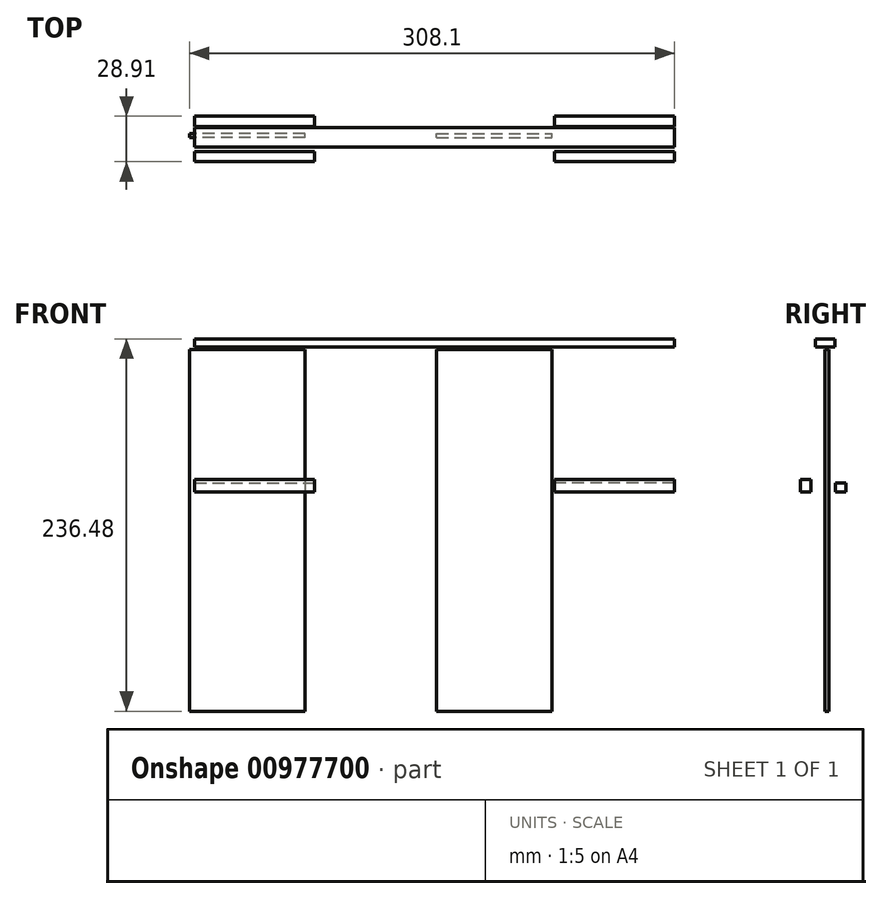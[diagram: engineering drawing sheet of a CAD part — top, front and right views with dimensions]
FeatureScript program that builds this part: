
annotation { "Feature Type Name" : "Feature", "Feature Type Description" : "" }
export const myFeature = defineFeature(function(context is Context, id is Id, definition is map)
    precondition{}
    {
        {
            var Q0;
            Q0=qCreatedBy(makeId("Front.planeOp"),FACE);
            var sketch = newSketch(context, id + "F0", { "sketchPlane" : qUnion([Q0])});
            skLineSegment(sketch, "E0.bottom", {"start": v(-73.47, 110.17) * mm, "end": v(0, 110.17) * mm});
            skLineSegment(sketch, "E0.top", {"start": v(-73.47, -119.67) * mm, "end": v(0, -119.67) * mm});
            skLineSegment(sketch, "E0.left", {"start": v(-73.47, 110.17) * mm, "end": v(-73.47, -119.67) * mm});
            skLineSegment(sketch, "E0.right", {"start": v(0, 110.17) * mm, "end": v(0, -119.67) * mm});
            skLineSegment(sketch, "E1.left", {"start": v(122.15, 40.13) * mm, "end": v(122.15, 36.44) * mm});
            skLineSegment(sketch, "E1.right", {"start": v(0, 40.13) * mm, "end": v(0, 36.44) * mm});
            skSolve(sketch);
        }
        {
            var Q0;
            {var subQ1=sQuery(id+"F0.wireOp",EDGE,"E0.bottom");Q0=makeQuery(id+"F0.imprint","IMPRINT",FACE,{"disambiguationData":[TD([[makeQuery(id+"F0.imprint","IMPRINT",EDGE,{"derivedFrom":subQ1}),-1.0]])]});}
            extrude(context, id + "F1", {"entities" : qUnion([Q0]), "depth" : 2.54 * mm, "offsetDistance" : 25.4 * mm});
        }
        {
            var Q0;
            Q0=qCreatedBy(makeId("Right.planeOp"),FACE);
            var sketch = newSketch(context, id + "F2", { "sketchPlane" : qUnion([Q0])});
            skLineSegment(sketch, "E2.bottom", {"start": v(-8.62, 111.65) * mm, "end": v(3.84, 111.65) * mm});
            skLineSegment(sketch, "E2.top", {"start": v(-8.62, 116.81) * mm, "end": v(3.84, 116.81) * mm});
            skLineSegment(sketch, "E2.left", {"start": v(-8.62, 111.65) * mm, "end": v(-8.62, 116.81) * mm});
            skLineSegment(sketch, "E2.right", {"start": v(3.84, 111.65) * mm, "end": v(3.84, 116.81) * mm});
            skSolve(sketch);
        }
        {
            var Q0;
            Q0 = qSketchRegion(id + "F2", true);
            extrude(context, id + "F3", {"entities" : qUnion([Q0]), "depth" : 152.4 * mm, "offsetDistance" : 25.4 * mm});
        }
        {
            var Q0;
            Q0=makeQuery(id+"F3.opExtrude","SWEPT_BODY",BODY,{"disambiguationData":[OSD([sQuery(id+"F2.wireOp",EDGE,"E2.bottom"),sQuery(id+"F2.wireOp",EDGE,"E2.top"),sQuery(id+"F2.wireOp",EDGE,"E2.left"),sQuery(id+"F2.wireOp",EDGE,"E2.right")])]});
            transform(context, id + "F4", {"entities" : qUnion([Q0]), "transformType" : TransformType.TRANSLATION_3D, "dx" : -76.2 * mm, "dy" : 0 * mm, "dz" : 0 * mm, "makeCopy" : false});
        }
        {
            var Q0;
            Q0=qCreatedBy(makeId("Right.planeOp"),FACE);
            var sketch = newSketch(context, id + "F5", { "sketchPlane" : qUnion([Q0])});
            skLineSegment(sketch, "E3.bottom", {"start": v(4.24, 25.3) * mm, "end": v(10.88, 25.3) * mm});
            skLineSegment(sketch, "E3.top", {"start": v(4.24, 19.45) * mm, "end": v(10.88, 19.45) * mm});
            skLineSegment(sketch, "E3.left", {"start": v(4.24, 25.3) * mm, "end": v(4.24, 19.45) * mm});
            skLineSegment(sketch, "E3.right", {"start": v(10.88, 25.3) * mm, "end": v(10.88, 19.45) * mm});
            skLineSegment(sketch, "E4.bottom", {"start": v(-18.03, 27.65) * mm, "end": v(-11.39, 27.65) * mm});
            skLineSegment(sketch, "E4.top", {"start": v(-18.03, 19.45) * mm, "end": v(-11.39, 19.45) * mm});
            skLineSegment(sketch, "E4.left", {"start": v(-18.03, 27.65) * mm, "end": v(-18.03, 19.45) * mm});
            skLineSegment(sketch, "E4.right", {"start": v(-11.39, 27.65) * mm, "end": v(-11.39, 19.45) * mm});
            skSolve(sketch);
        }
        {
            var Q0;
            Q0 = qSketchRegion(id + "F5", true);
            extrude(context, id + "F6", {"entities" : qUnion([Q0]), "depth" : 76.2 * mm, "offsetDistance" : 25.4 * mm});
        }
        {
            var Q0;
            Q0=makeQuery(id+"F1.opExtrude","SWEPT_BODY",BODY,{"disambiguationData":[OSD([sQuery(id+"F0.wireOp",EDGE,"E0.bottom"),sQuery(id+"F0.wireOp",EDGE,"E0.top"),sQuery(id+"F0.wireOp",EDGE,"E0.left"),sQuery(id+"F0.wireOp",EDGE,"E0.right"),sQuery(id+"F0.wireOp",EDGE,"E1.right")])]});
            var Q1;
            Q1=makeQuery(id+"F6.opExtrude","SWEPT_BODY",BODY,{"disambiguationData":[OSD([sQuery(id+"F5.wireOp",EDGE,"E4.bottom"),sQuery(id+"F5.wireOp",EDGE,"E4.top"),sQuery(id+"F5.wireOp",EDGE,"E4.left"),sQuery(id+"F5.wireOp",EDGE,"E4.right")])]});
            var Q2;
            Q2=makeQuery(id+"F3.opExtrude","SWEPT_BODY",BODY,{"disambiguationData":[OSD([sQuery(id+"F2.wireOp",EDGE,"E2.bottom"),sQuery(id+"F2.wireOp",EDGE,"E2.top"),sQuery(id+"F2.wireOp",EDGE,"E2.left"),sQuery(id+"F2.wireOp",EDGE,"E2.right")])]});
            var Q3;
            Q3=makeQuery(id+"F6.opExtrude","SWEPT_BODY",BODY,{"disambiguationData":[OSD([sQuery(id+"F5.wireOp",EDGE,"E3.bottom"),sQuery(id+"F5.wireOp",EDGE,"E3.top"),sQuery(id+"F5.wireOp",EDGE,"E3.left"),sQuery(id+"F5.wireOp",EDGE,"E3.right")])]});
            transform(context, id + "F7", {"entities" : qUnion([Q0, Q1, Q2, Q3]), "transformType" : TransformType.TRANSLATION_3D, "dx" : 0 * mm, "dy" : 0 * mm, "dz" : 114.3 * mm, "makeCopy" : false});
        }
        {
            var Q0;
            Q0=makeQuery(id+"F6.opExtrude","SWEPT_BODY",BODY,{"disambiguationData":[OSD([sQuery(id+"F5.wireOp",EDGE,"E4.bottom"),sQuery(id+"F5.wireOp",EDGE,"E4.top"),sQuery(id+"F5.wireOp",EDGE,"E4.left"),sQuery(id+"F5.wireOp",EDGE,"E4.right")])]});
            var Q1;
            Q1=makeQuery(id+"F1.opExtrude","SWEPT_BODY",BODY,{"disambiguationData":[OSD([sQuery(id+"F0.wireOp",EDGE,"E0.bottom"),sQuery(id+"F0.wireOp",EDGE,"E0.top"),sQuery(id+"F0.wireOp",EDGE,"E0.left"),sQuery(id+"F0.wireOp",EDGE,"E0.right"),sQuery(id+"F0.wireOp",EDGE,"E1.right")])]});
            var Q2;
            Q2=makeQuery(id+"F3.opExtrude","SWEPT_BODY",BODY,{"disambiguationData":[OSD([sQuery(id+"F2.wireOp",EDGE,"E2.bottom"),sQuery(id+"F2.wireOp",EDGE,"E2.top"),sQuery(id+"F2.wireOp",EDGE,"E2.left"),sQuery(id+"F2.wireOp",EDGE,"E2.right")])]});
            var Q3;
            Q3=makeQuery(id+"F6.opExtrude","SWEPT_BODY",BODY,{"disambiguationData":[OSD([sQuery(id+"F5.wireOp",EDGE,"E3.bottom"),sQuery(id+"F5.wireOp",EDGE,"E3.top"),sQuery(id+"F5.wireOp",EDGE,"E3.left"),sQuery(id+"F5.wireOp",EDGE,"E3.right")])]});
            var Q4;
            Q4=makeQuery(id+"F3.opExtrude","CAP_FACE",FACE,{"disambiguationData":[OSD([sQuery(id+"F2.wireOp",EDGE,"E2.bottom"),sQuery(id+"F2.wireOp",EDGE,"E2.top"),sQuery(id+"F2.wireOp",EDGE,"E2.left"),sQuery(id+"F2.wireOp",EDGE,"E2.right")])],"isStart":true});
            mirror(context, id + "F8", {"operationType" : NewBodyOperationType.ADD, "entities" : qUnion([Q0, Q1, Q2, Q3]), "mirrorPlane" : qUnion([Q4])});
        }
        {
            var Q0;
            Q0=makeQuery(id+"F1.opExtrude","SWEPT_BODY",BODY,{"disambiguationData":[OSD([sQuery(id+"F0.wireOp",EDGE,"E0.bottom"),sQuery(id+"F0.wireOp",EDGE,"E0.top"),sQuery(id+"F0.wireOp",EDGE,"E0.left"),sQuery(id+"F0.wireOp",EDGE,"E0.right"),sQuery(id+"F0.wireOp",EDGE,"E1.right")])]});
            transform(context, id + "F9", {"entities" : qUnion([Q0]), "transformType" : TransformType.TRANSLATION_3D, "dx" : 76.2 * mm, "dy" : 0 * mm, "dz" : 0 * mm, "makeCopy" : false});
        }
        {
            var Q0;
            Q0=makeQuery(id+"F1.opExtrude","SWEPT_BODY",BODY,{"disambiguationData":[OSD([sQuery(id+"F0.wireOp",EDGE,"E0.bottom"),sQuery(id+"F0.wireOp",EDGE,"E0.top"),sQuery(id+"F0.wireOp",EDGE,"E0.left"),sQuery(id+"F0.wireOp",EDGE,"E0.right"),sQuery(id+"F0.wireOp",EDGE,"E1.right")])]});
            transform(context, id + "F10", {"entities" : qUnion([Q0]), "transformType" : TransformType.TRANSLATION_3D, "dx" : -77.72 * mm, "dy" : 0 * mm, "dz" : 0 * mm, "makeCopy" : false});
        }
        {
            var Q0;
            Q0=makeQuery(id+"F8.opPattern","COPY",BODY,{"derivedFrom":makeQuery(id+"F1.opExtrude","SWEPT_BODY",BODY,{"disambiguationData":[OSD([sQuery(id+"F0.wireOp",EDGE,"E0.bottom"),sQuery(id+"F0.wireOp",EDGE,"E0.top"),sQuery(id+"F0.wireOp",EDGE,"E0.left"),sQuery(id+"F0.wireOp",EDGE,"E0.right"),sQuery(id+"F0.wireOp",EDGE,"E1.right")])]}),"instanceName":"1"});
            transform(context, id + "F11", {"entities" : qUnion([Q0]), "transformType" : TransformType.TRANSLATION_3D, "dx" : -79.5 * mm, "dy" : 0 * mm, "dz" : 0 * mm, "makeCopy" : false});
        }
    });
